# Revit family: Curtain_Door_DORMA_ES200-ST-Flex-Green_2-Leaf
name_source: partatom
category: Türen
revit_build: Autodesk Revit Architecture 2016 (Build: 20150220_1215(x64)
units: mm (PartAtom-declared; Revit-internal decimal feet)

## family parameters
Beim Laden mit Abzugskörper schneiden = Nein
Gemeinsam genutzt = Nein
Immer vertikal = Ja
OmniClass-Nummer = 23.30.10.00
OmniClass-Titel = Doors
Raumberechnungspunkt = Nein

## types (1)
- ST Flex Green Double Door
    Analytische Konstruktion = <None>
    Dicke = 45 mm
    Door Panel Thickness = 45 mm
    Frame = Aluminium-Dorma Metal-Anodized Silver
    Funktion = Innen
    Glass Thickness = 6 mm  [stored 0.019685 ft]
    Glazing = Glass-Dorma Glazing-Clear
    Offset = 60 mm  [stored 0.19685 ft]
    _current revision = 1

note: [stored X ft] marks values corroborated as IEEE doubles in the binary element streams (Revit-internal decimal feet)

## geometry (parser evidence)
native form markers: Blend x4, Sweep x4
no freeform markers — native parametric forms only
